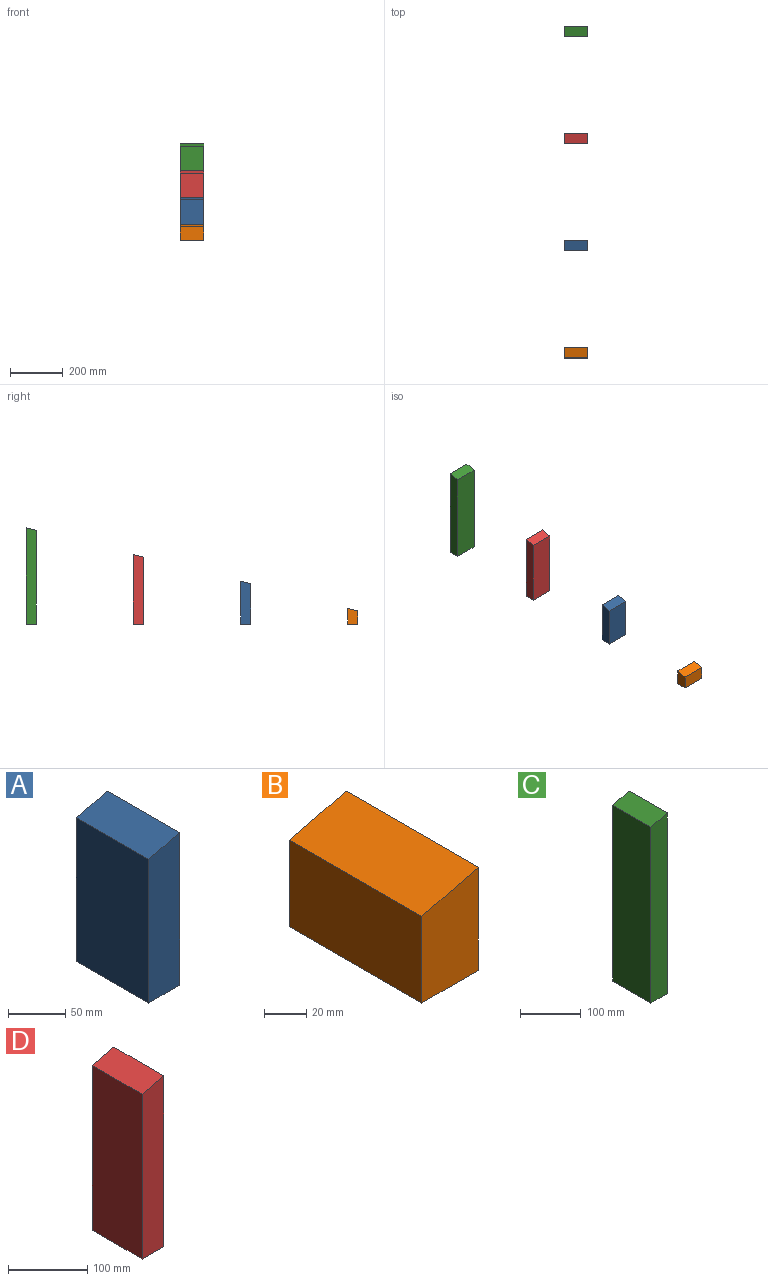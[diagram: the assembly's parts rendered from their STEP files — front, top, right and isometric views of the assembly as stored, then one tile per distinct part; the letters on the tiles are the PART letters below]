
ASSEMBLY  parts=4 mates=3
PART A: 6 faces, bbox 38.1x88.9x162.8 mm
  f0: plane 153.31x88.9mm, normal (-1,0,0), area 13629.7mm2, adj f1,f3,f4,f5
  f1: plane 162.81x38.1mm, normal (0,-1,0), area 6022.2mm2, adj f0,f2,f4,f5
  f2: plane 162.81x88.9mm, normal (1,0,0), area 14474.2mm2, adj f1,f3,f4,f5
  f3: plane 162.81x38.1mm, normal (0,1,0), area 6022.2mm2, adj f0,f2,f4,f5
  f4: plane 88.9x38.1mm, normal (0,0,-1), area 3387.1mm2, adj f0,f1,f2,f3
  f5: plane 88.9x38.1mm, normal (-0.24,0,0.97), area 3490.8mm2, adj f0,f1,f2,f3
PART B: 6 faces, bbox 38.1x88.9x59.9 mm
  f0: plane 88.9x50.44mm, normal (-1,0,0), area 4484.5mm2, adj f1,f3,f4,f5
  f1: plane 59.94x38.1mm, normal (0,-1,0), area 2102.9mm2, adj f0,f2,f4,f5
  f2: plane 88.9x59.94mm, normal (1,0,0), area 5329mm2, adj f1,f3,f4,f5
  f3: plane 59.94x38.1mm, normal (0,1,0), area 2102.9mm2, adj f0,f2,f4,f5
  f4: plane 88.9x38.1mm, normal (0,0,-1), area 3387.1mm2, adj f0,f1,f2,f3
  f5: plane 88.9x38.1mm, normal (-0.24,0,0.97), area 3490.8mm2, adj f0,f1,f2,f3
PART C: 6 faces, bbox 38.1x88.9x365.1 mm
  f0: plane 355.63x88.9mm, normal (-1,0,0), area 31615.1mm2, adj f1,f2,f4,f5
  f1: plane 365.13x38.1mm, normal (0,-1,0), area 13730.3mm2, adj f0,f3,f4,f5
  f2: plane 365.13x38.1mm, normal (0,1,0), area 13730.3mm2, adj f0,f3,f4,f5
  f3: plane 365.13x88.9mm, normal (1,0,0), area 32459.6mm2, adj f1,f2,f4,f5
  f4: plane 88.9x38.1mm, normal (0,0,-1), area 3387.1mm2, adj f0,f1,f2,f3
  f5: plane 88.9x38.1mm, normal (-0.24,0,0.97), area 3490.8mm2, adj f0,f1,f2,f3
PART D: 6 faces, bbox 38.1x88.9x263.5 mm
  f0: plane 254.03x88.9mm, normal (-1,0,0), area 22582.9mm2, adj f1,f3,f4,f5
  f1: plane 263.53x38.1mm, normal (0,-1,0), area 9859.3mm2, adj f0,f2,f4,f5
  f2: plane 263.53x88.9mm, normal (1,0,0), area 23427.4mm2, adj f1,f3,f4,f5
  f3: plane 263.53x38.1mm, normal (0,1,0), area 9859.3mm2, adj f0,f2,f4,f5
  f4: plane 88.9x38.1mm, normal (0,0,-1), area 3387.1mm2, adj f0,f1,f2,f3
  f5: plane 88.9x38.1mm, normal (-0.24,0,0.97), area 3490.8mm2, adj f0,f1,f2,f3
PLACE A rot(axis=(0,0,1),90deg) t=(44.45,1317.08,-1098.87)mm
PLACE B rot(axis=(0,0,1),90deg) t=(44.45,988.91,-1098.87)mm
PLACE C rot(axis=(0,0,1),90deg) t=(44.45,1963.26,-1098.87)mm
PLACE D rot(axis=(0,0,1),90deg) t=(44.45,1638.14,-1098.87)mm
MATE fastened D.f1 <-> C.f1  axis (1,0,0) through (44.45,1537.81,-1098.87)mm
MATE fastened A.f1 <-> B.f1  axis (1,0,0) through (44.45,1131.41,-1098.87)mm
MATE fastened D.f1 <-> A.f1  axis (1,0,0) through (44.45,1537.81,-1098.87)mm
